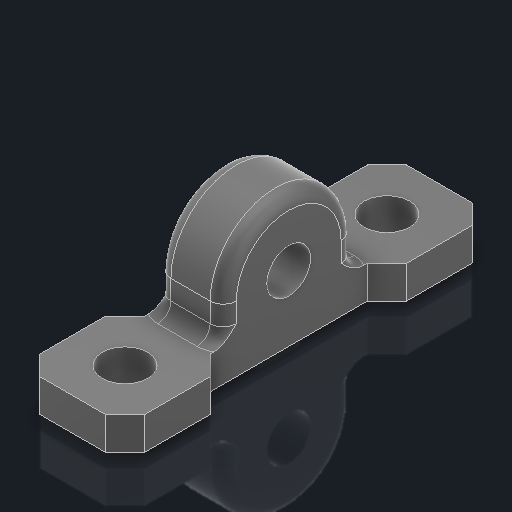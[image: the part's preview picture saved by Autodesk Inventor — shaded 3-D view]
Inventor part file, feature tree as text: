
AUTODESK INVENTOR PART (.ipt)
format: ipt  version: 2023.2 (Build 272271030, 271C)  size: 263,680 bytes
history: native  units: in
note: dims shown in document units (in); Inventor stores cm internally (conversion verified against a paired STEP export)
features: extrude x3, sketch x3, fillet x1
ambient origin geometry x8: Origin, YZ Plane, XZ Plane, XY Plane, X Axis, Y Axis, Z Axis, Center Point
bodies: Solid1 (feature_tree)
feature tree (7):
  extrude  "Extrusion1"  Depth=0.173in
  extrude  "Extrusion2"  Depth=0.4in
  extrude  "Extrusion3"  Depth=0.05in
  fillet  "Fillet1"  Radius=0.4in
  sketch  "Sketch1"  dims[d2=0.173in d3=0.173in]
  sketch  "Sketch2"  dims[d4=1.0in d8=0.4in]
  sketch  "Sketch3"  dims[d9=0.4in d10=0.4in d11=0.4in d12=0.6in d13=0.2in d14=0.2in d15=0.2in d16=0.25in d17=0.075in d18=0.075in d19=0.075in d20=0.075in d21=0.075in d22=0.075in d23=0.075in d24=0.075in d25=0.075in d26=0.075in d27=0.075in d28=0.075in d29=0.075in d30=0.075in d31=0.075in d32=0.075in d33=0.075in d34=0.125in d35=0.0in d36=0.176in d37=0.176in d38=0.037in d39=0.612in d40=0.02in d41=0.027in d42=0.0in d43=0.167in d44=0.25in d45=0.3in d46=0.5in d47=0.5in d48=0.25in d49=0.25in d50=0.027in d51=0.0in d52=0.05in]
